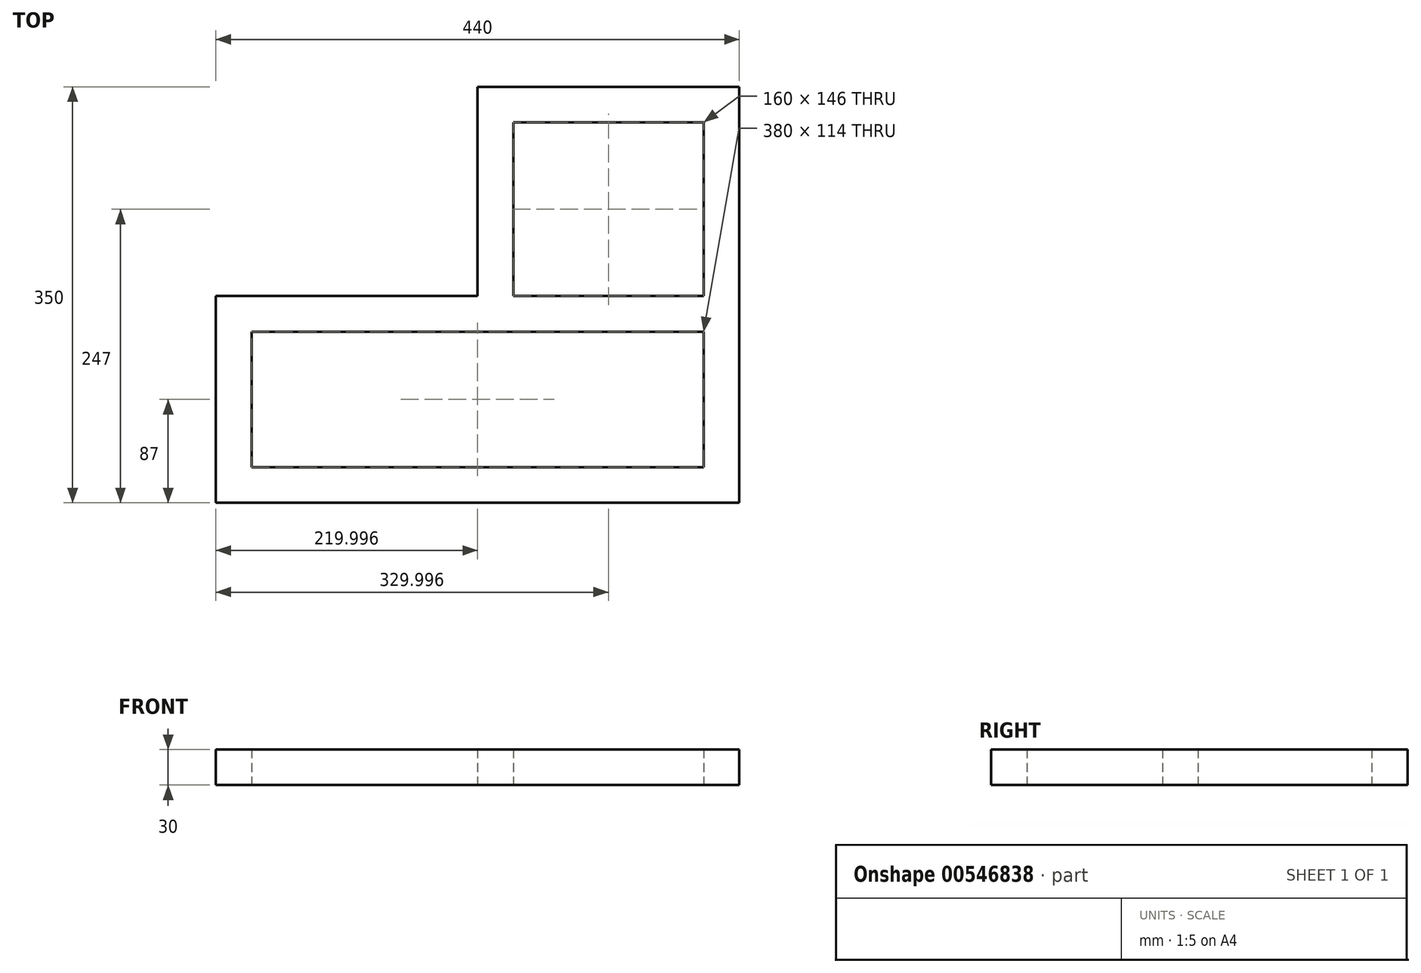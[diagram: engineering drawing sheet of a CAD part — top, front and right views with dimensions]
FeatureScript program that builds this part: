
annotation { "Feature Type Name" : "Feature", "Feature Type Description" : "" }
export const myFeature = defineFeature(function(context is Context, id is Id, definition is map)
    precondition{}
    {
        {
            var Q0;
            Q0=qCreatedBy(makeId("Top.planeOp"),FACE);
            var sketch = newSketch(context, id + "F0", { "sketchPlane" : qUnion([Q0])});
            skLineSegment(sketch, "E0.bottom", {"start": v(-40.04, -30) * mm, "end": v(-10.04, -30) * mm});
            skLineSegment(sketch, "E0.top", {"start": v(-40.04, 320) * mm, "end": v(-10.04, 320) * mm});
            skLineSegment(sketch, "E0.left", {"start": v(-40.04, -30) * mm, "end": v(-40.04, 320) * mm});
            skLineSegment(sketch, "E0.right", {"start": v(-10.04, -30) * mm, "end": v(-10.04, 320) * mm});
            skLineSegment(sketch, "E1.bottom", {"start": v(-40.04, -30) * mm, "end": v(-420.04, -30) * mm});
            skLineSegment(sketch, "E1.top", {"start": v(-40.04, 0) * mm, "end": v(-420.04, 0) * mm});
            skLineSegment(sketch, "E1.left", {"start": v(-40.04, -30) * mm, "end": v(-40.04, 0) * mm});
            skLineSegment(sketch, "E2", {"start": v(-420.04, 0) * mm, "end": v(-420.04, -30) * mm});
            skLineSegment(sketch, "E3.bottom", {"start": v(-420.04, -30) * mm, "end": v(-450.04, -30) * mm});
            skLineSegment(sketch, "E3.top", {"start": v(-420.04, 144) * mm, "end": v(-450.04, 144) * mm});
            skLineSegment(sketch, "E3.left", {"start": v(-420.04, -30) * mm, "end": v(-420.04, 144) * mm});
            skLineSegment(sketch, "E3.right", {"start": v(-450.04, -30) * mm, "end": v(-450.04, 144) * mm});
            skLineSegment(sketch, "E4.bottom", {"start": v(-420.04, 144) * mm, "end": v(-40.04, 144) * mm});
            skLineSegment(sketch, "E4.top", {"start": v(-420.04, 114) * mm, "end": v(-40.04, 114) * mm});
            skLineSegment(sketch, "E4.left", {"start": v(-420.04, 144) * mm, "end": v(-420.04, 114) * mm});
            skLineSegment(sketch, "E4.right", {"start": v(-40.04, 144) * mm, "end": v(-40.04, 114) * mm});
            skLineSegment(sketch, "E5.bottom", {"start": v(-40.04, 320) * mm, "end": v(-200.04, 320) * mm});
            skLineSegment(sketch, "E5.top", {"start": v(-40.04, 290) * mm, "end": v(-200.04, 290) * mm});
            skLineSegment(sketch, "E5.left", {"start": v(-40.04, 320) * mm, "end": v(-40.04, 290) * mm});
            skLineSegment(sketch, "E5.right", {"start": v(-200.04, 320) * mm, "end": v(-200.04, 290) * mm});
            skLineSegment(sketch, "E6.bottom", {"start": v(-200.04, 320) * mm, "end": v(-230.04, 320) * mm});
            skLineSegment(sketch, "E6.top", {"start": v(-200.04, 144) * mm, "end": v(-230.04, 144) * mm});
            skLineSegment(sketch, "E6.left", {"start": v(-200.04, 320) * mm, "end": v(-200.04, 144) * mm});
            skLineSegment(sketch, "E6.right", {"start": v(-230.04, 320) * mm, "end": v(-230.04, 144) * mm});
            skSolve(sketch);
        }
        {
            var Q0;
            Q0 = qSketchRegion(id + "F0", true);
            extrude(context, id + "F1", {"entities" : qUnion([Q0]), "depth" : 30 * mm, "offsetDistance" : 25 * mm});
        }
    });
